annotation { "Feature Type Name" : "Feature", "Feature Type Description" : "" }
export const myFeature = defineFeature(function(context is Context, id is Id, definition is map)
    precondition{}
    {
        {
            var Q0;
            Q0=qCreatedBy(makeId("Front.planeOp"),FACE);
            var sketch = newSketch(context, id + "F0", { "sketchPlane" : qUnion([Q0])});
            skLineSegment(sketch, "E0.bottom", {"start": v(0, 0) * mm, "end": v(66, 0) * mm});
            skLineSegment(sketch, "E0.top", {"start": v(0, 53) * mm, "end": v(64.5, 53) * mm});
            skLineSegment(sketch, "E0.left", {"start": v(0, 0) * mm, "end": v(0, 53) * mm});
            skPoint(sketch, "E1", {"position": v(66, 2.5) * mm});
            skPoint(sketch, "E2", {"position": v(66, 40) * mm});
            skLineSegment(sketch, "E3", {"start": v(66, 40) * mm, "end": v(68.47, 37.53) * mm});
            skLineSegment(sketch, "E4", {"start": v(66, 2.5) * mm, "end": v(68.47, 4.97) * mm});
            skLineSegment(sketch, "E5", {"start": v(66, 51.5) * mm, "end": v(66, 40) * mm});
            skLineSegment(sketch, "E6", {"start": v(66, 2.5) * mm, "end": v(66, 0) * mm});
            skLineSegment(sketch, "E7", {"start": v(68.47, 37.53) * mm, "end": v(68.47, 4.97) * mm});
            skPoint(sketch, "E8", {"position": v(66, 51.5) * mm});
            skPoint(sketch, "E9", {"position": v(64.5, 53) * mm});
            skLineSegment(sketch, "E10", {"start": v(64.5, 53) * mm, "end": v(66, 51.5) * mm});
            skPoint(sketch, "E11.orphan", {"position": v(66, 53) * mm});
            skCircle(sketch, "E12", {"center": v(65.47, 6.98) * mm, "radius": 2 * mm});
            skCircle(sketch, "E13", {"center": v(65.47, 35.5) * mm, "radius": 2 * mm});
            skCircle(sketch, "E14", {"center": v(14.5, 50) * mm, "radius": 2 * mm});
            skCircle(sketch, "E15", {"center": v(14.5, 3) * mm, "radius": 2 * mm});
            skLineSegment(sketch, "E16", {"start": v(66, 51.5) * mm, "end": v(66, 49.5) * mm});
            skLineSegment(sketch, "E17", {"start": v(66, 49.5) * mm, "end": v(65, 49.5) * mm});
            skSolve(sketch);
        }
        {
            var Q0;
            Q0=makeQuery(id+"F0.imprint","IMPRINT",FACE,{"disambiguationData":[TD([[makeQuery(id+"F0.imprint","IMPRINT",EDGE,{"derivedFrom":sQuery(id+"F0.wireOp",EDGE,"E0.bottom")}),1.0]])]});
            extrude(context, id + "F1", {"entities" : qUnion([Q0]), "depth" : 1.5 * mm});
        }
        {
            var Q0;
            Q0=makeQuery(id+"F1.opExtrude","CAP_FACE",FACE,{"disambiguationData":[OSD([sQuery(id+"F0.wireOp",EDGE,"E0.bottom"),sQuery(id+"F0.wireOp",EDGE,"E0.top"),sQuery(id+"F0.wireOp",EDGE,"E0.left"),sQuery(id+"F0.wireOp",EDGE,"E3"),sQuery(id+"F0.wireOp",EDGE,"E4"),sQuery(id+"F0.wireOp",EDGE,"E5"),sQuery(id+"F0.wireOp",EDGE,"E6"),sQuery(id+"F0.wireOp",EDGE,"E7"),sQuery(id+"F0.wireOp",EDGE,"E10"),sQuery(id+"F0.wireOp",EDGE,"E12"),sQuery(id+"F0.wireOp",EDGE,"E13"),sQuery(id+"F0.wireOp",EDGE,"E14"),sQuery(id+"F0.wireOp",EDGE,"E15"),sQuery(id+"F0.wireOp",EDGE,"E16")])],"isStart":false});
            var sketch = newSketch(context, id + "F2", { "sketchPlane" : qUnion([Q0])});
            skLineSegment(sketch, "E18.bottom", {"start": v(64.5, 51.5) * mm, "end": v(43.5, 51.5) * mm});
            skLineSegment(sketch, "E18.top", {"start": v(64.5, 49.5) * mm, "end": v(43.5, 49.5) * mm});
            skLineSegment(sketch, "E18.left", {"start": v(64.5, 51.5) * mm, "end": v(64.5, 49.5) * mm});
            skLineSegment(sketch, "E18.right", {"start": v(43.5, 51.5) * mm, "end": v(43.5, 49.5) * mm});
            skLineSegment(sketch, "E19.bottom", {"start": v(42, 51.5) * mm, "end": v(21, 51.5) * mm});
            skLineSegment(sketch, "E19.top", {"start": v(42, 49.5) * mm, "end": v(21, 49.5) * mm});
            skLineSegment(sketch, "E19.left", {"start": v(42, 51.5) * mm, "end": v(42, 49.5) * mm});
            skLineSegment(sketch, "E19.right", {"start": v(21, 51.5) * mm, "end": v(21, 49.5) * mm});
            skLineSegment(sketch, "E20", {"start": v(64.5, 48.83) * mm, "end": v(64.5, 1.5) * mm, "construction": true});
            skLineSegment(sketch, "E21", {"start": v(64.5, 1.5) * mm, "end": v(31.33, 1.5) * mm, "construction": true});
            skLineSegment(sketch, "E22.bottom", {"start": v(64.5, 1.5) * mm, "end": v(48.5, 1.5) * mm});
            skLineSegment(sketch, "E22.top", {"start": v(64.5, 3.5) * mm, "end": v(48.5, 3.5) * mm});
            skLineSegment(sketch, "E22.left", {"start": v(64.5, 1.5) * mm, "end": v(64.5, 3.5) * mm});
            skLineSegment(sketch, "E22.right", {"start": v(48.5, 1.5) * mm, "end": v(48.5, 3.5) * mm});
            skLineSegment(sketch, "E23.bottom", {"start": v(47, 1.5) * mm, "end": v(31, 1.5) * mm});
            skLineSegment(sketch, "E23.top", {"start": v(47, 3.48) * mm, "end": v(31, 3.48) * mm});
            skLineSegment(sketch, "E23.left", {"start": v(47, 1.5) * mm, "end": v(47, 3.48) * mm});
            skLineSegment(sketch, "E23.right", {"start": v(31, 1.5) * mm, "end": v(31, 3.48) * mm});
            skSolve(sketch);
        }
        {
            var Q0;
            Q0 = qSketchRegion(id + "F2", true);
            extrude(context, id + "F3", {"entities" : qUnion([Q0]), "operationType" : NewBodyOperationType.ADD, "depth" : 8 * mm});
        }
        {
            var Q0;
            Q0=makeQuery(id+"F1.opExtrude","CAP_FACE",FACE,{"disambiguationData":[OSD([sQuery(id+"F0.wireOp",EDGE,"E0.bottom"),sQuery(id+"F0.wireOp",EDGE,"E0.top"),sQuery(id+"F0.wireOp",EDGE,"E0.left"),sQuery(id+"F0.wireOp",EDGE,"E3"),sQuery(id+"F0.wireOp",EDGE,"E4"),sQuery(id+"F0.wireOp",EDGE,"E5"),sQuery(id+"F0.wireOp",EDGE,"E6"),sQuery(id+"F0.wireOp",EDGE,"E7"),sQuery(id+"F0.wireOp",EDGE,"E10"),sQuery(id+"F0.wireOp",EDGE,"E12"),sQuery(id+"F0.wireOp",EDGE,"E13"),sQuery(id+"F0.wireOp",EDGE,"E14"),sQuery(id+"F0.wireOp",EDGE,"E15"),sQuery(id+"F0.wireOp",EDGE,"E16")])],"isStart":false});
            var sketch = newSketch(context, id + "F4", { "sketchPlane" : qUnion([Q0])});
            skLineSegment(sketch, "E24.bottom", {"start": v(0, 4) * mm, "end": v(11, 4) * mm});
            skLineSegment(sketch, "E24.top", {"start": v(0, 12) * mm, "end": v(11, 12) * mm});
            skLineSegment(sketch, "E24.left", {"start": v(0, 4) * mm, "end": v(0, 12) * mm});
            skLineSegment(sketch, "E24.right", {"start": v(11, 4) * mm, "end": v(11, 12) * mm});
            skSolve(sketch);
        }
        {
            var Q0;
            Q0=makeQuery(id+"F4.imprint","IMPRINT",FACE,{"disambiguationData":[TD([[makeQuery(id+"F4.imprint","IMPRINT",EDGE,{"derivedFrom":sQuery(id+"F4.wireOp",EDGE,"E24.bottom")}),1.0]])]});
            extrude(context, id + "F5", {"entities" : qUnion([Q0]), "operationType" : NewBodyOperationType.ADD, "depth" : 9 * mm});
        }
        {
            var Q0;
            Q0=makeQuery(id+"F5.boolean.opBoolean","MERGE",FACE,{"derivedFrom":[makeQuery(id+"F1.opExtrude","SWEPT_FACE",FACE,{"disambiguationData":[OSD([sQuery(id+"F0.wireOp",EDGE,"E0.left")])]}),makeQuery(id+"F5.opExtrude","SWEPT_FACE",FACE,{"disambiguationData":[OSD([sQuery(id+"F4.wireOp",EDGE,"E24.left")])]})]});
            var sketch = newSketch(context, id + "F6", { "sketchPlane" : qUnion([Q0])});
            skLineSegment(sketch, "E25.bottom", {"start": v(10.5, 12) * mm, "end": v(1.5, 12) * mm});
            skLineSegment(sketch, "E25.top", {"start": v(10.5, 4) * mm, "end": v(1.5, 4) * mm});
            skLineSegment(sketch, "E25.left", {"start": v(10.5, 12) * mm, "end": v(10.5, 4) * mm});
            skLineSegment(sketch, "E25.right", {"start": v(1.5, 12) * mm, "end": v(1.5, 4) * mm});
            skLineSegment(sketch, "E26", {"start": v(6.5, 12) * mm, "end": v(6.5, 10.75) * mm});
            skCircle(sketch, "E27", {"center": v(6.5, 8) * mm, "radius": 2.75 * mm});
            skLineSegment(sketch, "E28.trimOffspring", {"start": v(6.5, 5.25) * mm, "end": v(6.5, 4) * mm});
            skSolve(sketch);
        }
        {
            var Q0;
            Q0 = qSketchRegion(id + "F6", true);
            extrude(context, id + "F7", {"entities" : qUnion([Q0]), "operationType" : NewBodyOperationType.ADD, "depth" : 4 * mm});
        }
        {
            var Q0;
            Q0=makeQuery(id+"F1.opExtrude","CAP_FACE",FACE,{"disambiguationData":[OSD([sQuery(id+"F0.wireOp",EDGE,"E0.bottom"),sQuery(id+"F0.wireOp",EDGE,"E0.top"),sQuery(id+"F0.wireOp",EDGE,"E0.left"),sQuery(id+"F0.wireOp",EDGE,"E3"),sQuery(id+"F0.wireOp",EDGE,"E4"),sQuery(id+"F0.wireOp",EDGE,"E5"),sQuery(id+"F0.wireOp",EDGE,"E6"),sQuery(id+"F0.wireOp",EDGE,"E7"),sQuery(id+"F0.wireOp",EDGE,"E10"),sQuery(id+"F0.wireOp",EDGE,"E12"),sQuery(id+"F0.wireOp",EDGE,"E13"),sQuery(id+"F0.wireOp",EDGE,"E14"),sQuery(id+"F0.wireOp",EDGE,"E15"),sQuery(id+"F0.wireOp",EDGE,"E16")])],"isStart":false});
            var sketch = newSketch(context, id + "F8", { "sketchPlane" : qUnion([Q0])});
            skLineSegment(sketch, "E29.bottom", {"start": v(0, 44) * mm, "end": v(6, 44) * mm});
            skLineSegment(sketch, "E29.top", {"start": v(0, 37) * mm, "end": v(6, 37) * mm});
            skLineSegment(sketch, "E29.left", {"start": v(0, 44) * mm, "end": v(0, 37) * mm});
            skLineSegment(sketch, "E29.right", {"start": v(6, 44) * mm, "end": v(6, 37) * mm});
            skSolve(sketch);
        }
        {
            var Q0;
            Q0 = qSketchRegion(id + "F8", true);
            extrude(context, id + "F9", {"entities" : qUnion([Q0]), "operationType" : NewBodyOperationType.ADD, "depth" : 2.5 * mm});
        }
        {
            var Q0;
            {var subQ12=sQuery(id+"F0.wireOp",EDGE,"E0.left");var subQ13=sQuery(id+"F0.wireOp",EDGE,"E0.bottom");Q0=makeQuery(id+"F9.boolean.opBoolean","MERGE",FACE,{"derivedFrom":[makeQuery(id+"F7.boolean.opBoolean","SPLIT",FACE,{"disambiguationData":[TD([makeQuery(id+"F1.opExtrude","SWEPT_FACE",FACE,{"disambiguationData":[OSD([subQ13])]})])],"derivedFrom":makeQuery(id+"F5.boolean.opBoolean","MERGE",FACE,{"derivedFrom":[makeQuery(id+"F1.opExtrude","SWEPT_FACE",FACE,{"disambiguationData":[OSD([subQ12])]}),makeQuery(id+"F5.opExtrude","SWEPT_FACE",FACE,{"disambiguationData":[OSD([sQuery(id+"F4.wireOp",EDGE,"E24.left")])]})]})}),makeQuery(id+"F9.opExtrude","SWEPT_FACE",FACE,{"disambiguationData":[OSD([sQuery(id+"F8.wireOp",EDGE,"E29.left")])]})]});}
            var sketch = newSketch(context, id + "F10", { "sketchPlane" : qUnion([Q0])});
            skLineSegment(sketch, "E30.bottom", {"start": v(4, 37) * mm, "end": v(1.5, 37) * mm});
            skLineSegment(sketch, "E30.top", {"start": v(4, 44) * mm, "end": v(1.5, 44) * mm});
            skLineSegment(sketch, "E30.left", {"start": v(4, 37) * mm, "end": v(4, 44) * mm});
            skLineSegment(sketch, "E30.right", {"start": v(1.5, 37) * mm, "end": v(1.5, 44) * mm});
            skLineSegment(sketch, "E31", {"start": v(3.5, 43.5) * mm, "end": v(3.5, 37.5) * mm});
            skLineSegment(sketch, "E32", {"start": v(3.5, 37.5) * mm, "end": v(2.5, 37.5) * mm});
            skLineSegment(sketch, "E33", {"start": v(2.5, 37.5) * mm, "end": v(2, 38) * mm});
            skLineSegment(sketch, "E34", {"start": v(2, 38) * mm, "end": v(2, 43) * mm});
            skLineSegment(sketch, "E35", {"start": v(2, 43) * mm, "end": v(2.5, 43.5) * mm});
            skLineSegment(sketch, "E36", {"start": v(2.5, 43.5) * mm, "end": v(3.5, 43.5) * mm});
            skSolve(sketch);
        }
        {
            var Q0;
            Q0 = qSketchRegion(id + "F10", true);
            extrude(context, id + "F11", {"entities" : qUnion([Q0]), "operationType" : NewBodyOperationType.ADD, "depth" : 3 * mm});
        }
        {
            var Q0;
            Q0=makeQuery(id+"F1.opExtrude","CAP_FACE",FACE,{"disambiguationData":[OSD([sQuery(id+"F0.wireOp",EDGE,"E0.bottom"),sQuery(id+"F0.wireOp",EDGE,"E0.top"),sQuery(id+"F0.wireOp",EDGE,"E0.left"),sQuery(id+"F0.wireOp",EDGE,"E3"),sQuery(id+"F0.wireOp",EDGE,"E4"),sQuery(id+"F0.wireOp",EDGE,"E5"),sQuery(id+"F0.wireOp",EDGE,"E6"),sQuery(id+"F0.wireOp",EDGE,"E7"),sQuery(id+"F0.wireOp",EDGE,"E10"),sQuery(id+"F0.wireOp",EDGE,"E12"),sQuery(id+"F0.wireOp",EDGE,"E13"),sQuery(id+"F0.wireOp",EDGE,"E14"),sQuery(id+"F0.wireOp",EDGE,"E15"),sQuery(id+"F0.wireOp",EDGE,"E16")])],"isStart":true});
            var sketch = newSketch(context, id + "F12", { "sketchPlane" : qUnion([Q0])});
            skText(sketch, "E37", { "text": "Adam Ardeishar", "fontName": "OpenSans-Regular.ttf"});
            skText(sketch, "E38", { "text": "Andrew Nam", "fontName": "OpenSans-Regular.ttf"});
            const initialGuessF12  = {"E37": [-0.06, 0.043, 1, 0, 0.005], "E38": [-0.06, 0.033, 1, 0, 0.005]};
            skSetInitialGuess(sketch, initialGuessF12);
            skSolve(sketch);
        }
        {
            var Q0;
            Q0 = qSketchRegion(id + "F12", true);
            extrude(context, id + "F13", {"entities" : qUnion([Q0]), "operationType" : NewBodyOperationType.ADD, "depth" : 0.1 * mm});
        }
        {
            var Q0;
            Q0=makeQuery(id+"F1.opExtrude","CAP_FACE",FACE,{"disambiguationData":[OSD([sQuery(id+"F0.wireOp",EDGE,"E0.bottom"),sQuery(id+"F0.wireOp",EDGE,"E0.top"),sQuery(id+"F0.wireOp",EDGE,"E0.left"),sQuery(id+"F0.wireOp",EDGE,"E3"),sQuery(id+"F0.wireOp",EDGE,"E4"),sQuery(id+"F0.wireOp",EDGE,"E5"),sQuery(id+"F0.wireOp",EDGE,"E6"),sQuery(id+"F0.wireOp",EDGE,"E7"),sQuery(id+"F0.wireOp",EDGE,"E10"),sQuery(id+"F0.wireOp",EDGE,"E12"),sQuery(id+"F0.wireOp",EDGE,"E13"),sQuery(id+"F0.wireOp",EDGE,"E14"),sQuery(id+"F0.wireOp",EDGE,"E15"),sQuery(id+"F0.wireOp",EDGE,"E16")])],"isStart":false});
            var sketch = newSketch(context, id + "F14", { "sketchPlane" : qUnion([Q0])});
            skLineSegment(sketch, "E39.bottom", {"start": v(63.47, 10) * mm, "end": v(28.47, 10) * mm});
            skLineSegment(sketch, "E39.top", {"start": v(63.47, 18) * mm, "end": v(28.47, 18) * mm});
            skLineSegment(sketch, "E39.left", {"start": v(63.47, 10) * mm, "end": v(63.47, 18) * mm});
            skLineSegment(sketch, "E39.right", {"start": v(28.47, 10) * mm, "end": v(28.47, 18) * mm});
            skSolve(sketch);
        }
        {
            var Q0;
            Q0 = qSketchRegion(id + "F14", true);
            extrude(context, id + "F15", {"entities" : qUnion([Q0]), "operationType" : NewBodyOperationType.ADD, "depth" : 6 * mm});
        }
        {
            var Q0;
            Q0=makeQuery(id+"F1.opExtrude","CAP_FACE",FACE,{"disambiguationData":[OSD([sQuery(id+"F0.wireOp",EDGE,"E0.bottom"),sQuery(id+"F0.wireOp",EDGE,"E0.top"),sQuery(id+"F0.wireOp",EDGE,"E0.left"),sQuery(id+"F0.wireOp",EDGE,"E3"),sQuery(id+"F0.wireOp",EDGE,"E4"),sQuery(id+"F0.wireOp",EDGE,"E5"),sQuery(id+"F0.wireOp",EDGE,"E6"),sQuery(id+"F0.wireOp",EDGE,"E7"),sQuery(id+"F0.wireOp",EDGE,"E10"),sQuery(id+"F0.wireOp",EDGE,"E12"),sQuery(id+"F0.wireOp",EDGE,"E13"),sQuery(id+"F0.wireOp",EDGE,"E14"),sQuery(id+"F0.wireOp",EDGE,"E15"),sQuery(id+"F0.wireOp",EDGE,"E16")])],"isStart":false});
            var sketch = newSketch(context, id + "F16", { "sketchPlane" : qUnion([Q0])});
            skLineSegment(sketch, "E40.bottom", {"start": v(56.47, 22) * mm, "end": v(50.97, 22) * mm});
            skLineSegment(sketch, "E40.top", {"start": v(56.47, 27.5) * mm, "end": v(50.97, 27.5) * mm});
            skLineSegment(sketch, "E40.left", {"start": v(56.47, 22) * mm, "end": v(56.47, 27.5) * mm});
            skLineSegment(sketch, "E40.right", {"start": v(50.97, 22) * mm, "end": v(50.97, 27.5) * mm});
            skSolve(sketch);
        }
        {
            var Q0;
            Q0 = qSketchRegion(id + "F16", true);
            extrude(context, id + "F17", {"entities" : qUnion([Q0]), "operationType" : NewBodyOperationType.ADD, "depth" : 3 * mm});
        }
        {
            var Q0;
            Q0=makeQuery(id+"F17.opExtrude","CAP_FACE",FACE,{"disambiguationData":[OSD([sQuery(id+"F16.wireOp",EDGE,"E40.bottom"),sQuery(id+"F16.wireOp",EDGE,"E40.top"),sQuery(id+"F16.wireOp",EDGE,"E40.left"),sQuery(id+"F16.wireOp",EDGE,"E40.right")])],"isStart":false});
            var sketch = newSketch(context, id + "F18", { "sketchPlane" : qUnion([Q0])});
            skCircle(sketch, "E41", {"center": v(53.72, 24.75) * mm, "radius": 2.25 * mm});
            skPoint(sketch, "E41.centerSnap0", {"position": v(53.72, 27.5) * mm});
            skSolve(sketch);
        }
        {
            var Q0;
            Q0 = qSketchRegion(id + "F18", true);
            extrude(context, id + "F19", {"entities" : qUnion([Q0]), "operationType" : NewBodyOperationType.ADD, "depth" : 3 * mm});
        }
    });